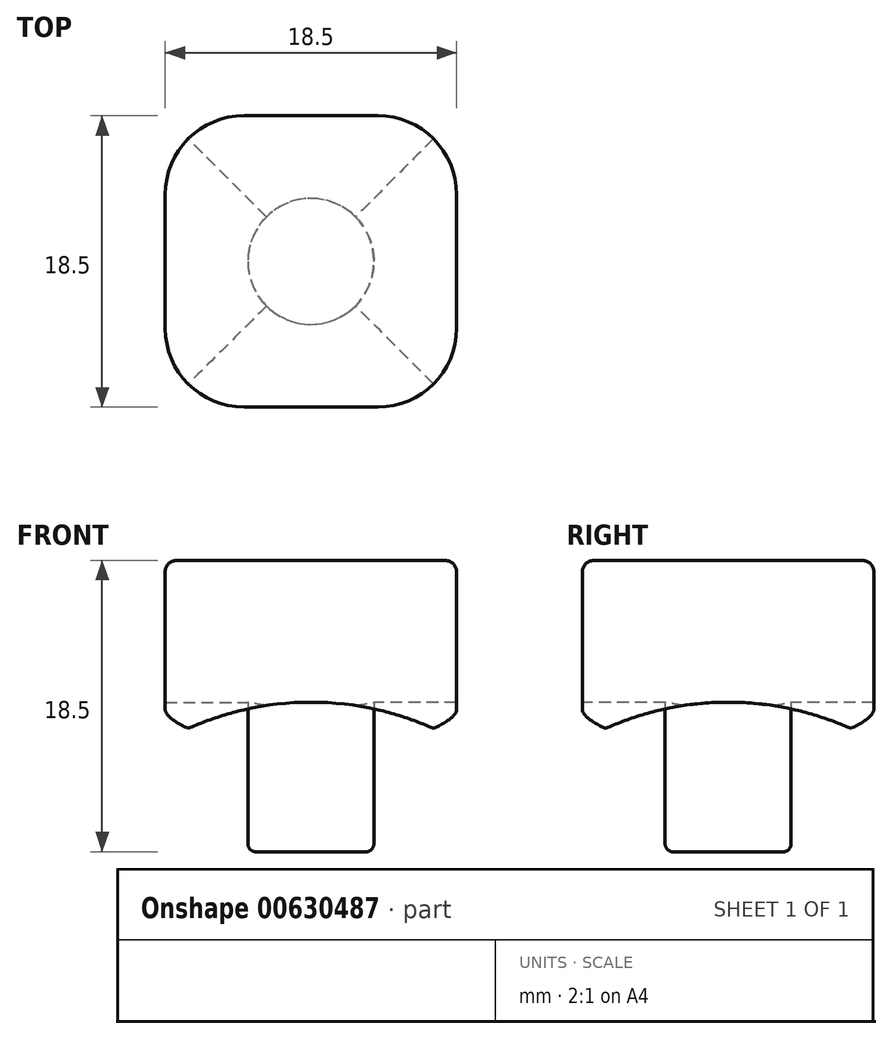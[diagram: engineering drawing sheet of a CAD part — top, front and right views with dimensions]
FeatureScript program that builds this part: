
annotation { "Feature Type Name" : "Feature", "Feature Type Description" : "" }
export const myFeature = defineFeature(function(context is Context, id is Id, definition is map)
    precondition{}
    {
        {
            var Q0;
            Q0=qCreatedBy(makeId("Front.planeOp"),FACE);
            var sketch = newSketch(context, id + "F0", { "sketchPlane" : qUnion([Q0])});
            skLineSegment(sketch, "E0.rect.bottom", {"start": v(9.25, 5.5) * mm, "end": v(-9.25, 5.5) * mm});
            skLineSegment(sketch, "E0.rect.top", {"start": v(9.25, -5.5) * mm, "end": v(-9.25, -5.5) * mm});
            skLineSegment(sketch, "E0.rect.left", {"start": v(9.25, 5.5) * mm, "end": v(9.25, -5.5) * mm});
            skLineSegment(sketch, "E0.rect.right", {"start": v(-9.25, 5.5) * mm, "end": v(-9.25, -5.5) * mm});
            skPoint(sketch, "E0.rect.middle", {"position": v(0, 0) * mm});
            skSolve(sketch);
        }
        {
            var Q0;
            Q0=makeQuery(id+"F0.imprint","IMPRINT",FACE,{"disambiguationData":[TD([[makeQuery(id+"F0.imprint","IMPRINT",EDGE,{"derivedFrom":sQuery(id+"F0.wireOp",EDGE,"E0.rect.bottom")}),1.0]])]});
            extrude(context, id + "F1", {"entities" : qUnion([Q0]), "oppositeDirection" : true, "depth" : 9.25 * mm});
        }
        {
            var Q0;
            Q0=qSketchRegion(id+"F0",true);
            extrude(context, id + "F2", {"entities" : qUnion([Q0]), "operationType" : NewBodyOperationType.ADD, "depth" : 9.25 * mm});
        }
        {
            var Q0;
            Q0=qCreatedBy(makeId("Front.planeOp"),FACE);
            var sketch = newSketch(context, id + "F3", { "sketchPlane" : qUnion([Q0])});
            skPoint(sketch, "E1", {"position": v(0, -3.5) * mm});
            skCircle(sketch, "E2", {"center": v(0, -22.5) * mm, "radius": 19 * mm});
            skSolve(sketch);
        }
        {
            var Q0;
            Q0=qCreatedBy(makeId("Right.planeOp"),FACE);
            var sketch = newSketch(context, id + "F4", { "sketchPlane" : qUnion([Q0])});
            skPoint(sketch, "E3", {"position": v(0, -3.5) * mm});
            skCircle(sketch, "E4", {"center": v(0, -22.5) * mm, "radius": 19 * mm});
            skSolve(sketch);
        }
        {
            var Q0;
            Q0=qSketchRegion(id+"F9",true);
            var Q1;
            Q1=qSketchRegion(id+"F3",true);
            extrude(context, id + "F5", {"entities" : qUnion([Q0, Q1]), "operationType" : NewBodyOperationType.REMOVE, "oppositeDirection" : true, "depth" : 25.4 * mm});
        }
        {
            var Q0;
            Q0=qSketchRegion(id+"F3",true);
            extrude(context, id + "F6", {"entities" : qUnion([Q0]), "operationType" : NewBodyOperationType.REMOVE, "depth" : 25.4 * mm});
        }
        {
            var Q0;
            Q0=qSketchRegion(id+"F4",true);
            extrude(context, id + "F7", {"entities" : qUnion([Q0]), "operationType" : NewBodyOperationType.REMOVE, "oppositeDirection" : true, "depth" : 25.4 * mm});
        }
        {
            var Q0;
            Q0=qSketchRegion(id+"F4",true);
            extrude(context, id + "F8", {"entities" : qUnion([Q0]), "operationType" : NewBodyOperationType.REMOVE, "depth" : 25.4 * mm});
        }
        {
            var Q0;
            {var subQ0=sQuery(id+"F0.wireOp",EDGE,"E0.rect.top");Q0=makeQuery(id+"F2.boolean.opBoolean","MERGE",FACE,{"derivedFrom":[makeQuery(id+"F1.opExtrude","SWEPT_FACE",FACE,{"disambiguationData":[OSD([subQ0])]}),makeQuery(id+"F2.opExtrude","SWEPT_FACE",FACE,{"disambiguationData":[OSD([subQ0])]})]});}
            var sketch = newSketch(context, id + "F9", { "sketchPlane" : qUnion([Q0])});
            skCircle(sketch, "E5", {"center": v(0, 0) * mm, "radius": 4 * mm});
            skSolve(sketch);
        }
        {
            var Q0;
            Q0=qSketchRegion(id+"F9",true);
            extrude(context, id + "F10", {"entities" : qUnion([Q0]), "operationType" : NewBodyOperationType.ADD, "oppositeDirection" : true, "depth" : 3.46 * mm});
        }
        {
            var Q0;
            Q0=makeQuery(id+"F10.opExtrude","CAP_FACE",FACE,{"disambiguationData":[OSD([sQuery(id+"F9.wireOp",EDGE,"E5")])],"isStart":true});
            extrude(context, id + "F11", {"entities" : qUnion([Q0]), "operationType" : NewBodyOperationType.ADD, "depth" : 7.5 * mm});
        }
        {
            var Q0;
            Q0=makeQuery(id+"F2.opExtrude","CAP_EDGE",EDGE,{"disambiguationData":[OSD([sQuery(id+"F0.wireOp",EDGE,"E0.rect.right")])],"isStart":false});
            var Q1;
            Q1=makeQuery(id+"F1.opExtrude","CAP_EDGE",EDGE,{"disambiguationData":[OSD([sQuery(id+"F0.wireOp",EDGE,"E0.rect.right")])],"isStart":false});
            var Q2;
            Q2=makeQuery(id+"F1.opExtrude","CAP_EDGE",EDGE,{"disambiguationData":[OSD([sQuery(id+"F0.wireOp",EDGE,"E0.rect.left")])],"isStart":false});
            var Q3;
            Q3=makeQuery(id+"F2.opExtrude","CAP_EDGE",EDGE,{"disambiguationData":[OSD([sQuery(id+"F0.wireOp",EDGE,"E0.rect.left")])],"isStart":false});
            fillet(context, id + "F12", {"entities" : qUnion([Q0, Q1, Q2, Q3]), "radius" : 5 * mm, "tangentPropagation" : true, "allowEdgeOverflow" : false});
        }
        {
            var Q0;
            {var subQ0=sQuery(id+"F0.wireOp",EDGE,"E0.rect.bottom");Q0=makeQuery(id+"F2.boolean.opBoolean","MERGE",FACE,{"derivedFrom":[makeQuery(id+"F1.opExtrude","SWEPT_FACE",FACE,{"disambiguationData":[OSD([subQ0])]}),makeQuery(id+"F2.opExtrude","SWEPT_FACE",FACE,{"disambiguationData":[OSD([subQ0])]})]});}
            fillet(context, id + "F13", {"entities" : qUnion([Q0]), "radius" : 0.7 * mm, "tangentPropagation" : true, "allowEdgeOverflow" : false});
        }
        {
            var Q0;
            Q0=makeQuery(id+"F11.opExtrude","CAP_FACE",FACE,{"disambiguationData":[OSD([sQuery(id+"F9.wireOp",EDGE,"E5")])],"isStart":false});
            fillet(context, id + "F14", {"entities" : qUnion([Q0]), "radius" : 0.5 * mm, "tangentPropagation" : true, "allowEdgeOverflow" : false});
        }
    });
